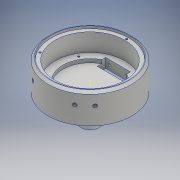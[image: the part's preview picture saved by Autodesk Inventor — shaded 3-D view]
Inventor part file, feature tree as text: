
AUTODESK INVENTOR PART (.ipt)
format: ipt  version: 2017 (Build 210142000, 142)  size: 281,088 bytes
history: native  units: mm
features: sketch x14, thread x10, extrude x7, plane x7, hole x7, projected_geometry x2, chamfer x1
ambient origin geometry x8: Origin, YZ Plane, XZ Plane, XY Plane, X Axis, Y Axis, Z Axis, Center Point
bodies: Solid1 (feature_tree)
feature tree (48):
  extrude  "Extrusion1"  Depth=25.0mm TaperAngle=0.0deg
  extrude  "Extrusion2"  Depth=17.0mm TaperAngle=0.0deg
  extrude  "Extrusion4"  Depth=35.0mm
  plane  "Work Plane1"
  extrude  "Extrusion7"  Depth=2.0mm TaperAngle=0.0deg
  chamfer  "Chamfer1"  Distance=2.0mm Angle=45.0deg
  hole  "Hole3"  [1 undecoded]
  hole  "Hole4"  [1 undecoded]
  thread  "Thread1"  [1 undecoded]
  thread  "Thread2"  [1 undecoded]
  thread  "Thread3"  [1 undecoded]
  thread  "Thread4"  [1 undecoded]
  thread  "Thread5"  [1 undecoded]
  thread  "Thread6"  [1 undecoded]
  sketch  "Sketch12"  dims[d54=1.6mm d55=6.0mm d56=4.0mm d57=2.0mm d58=90.0deg d59=5.0mm d60=20.594885mm d61=61.315mm d62=30.0mm d64=360.0deg]
  plane  "Work Plane2"
  plane  "Work Plane3"
  plane  "Work Plane4"
  plane  "Work Plane5"
  hole  "Hole5"  [1 undecoded]
  hole  "Hole6"  [1 undecoded]
  hole  "Hole9"  [1 undecoded]
  hole  "Hole10"  [1 undecoded]
  thread  "Thread7"  [1 undecoded]
  thread  "Thread8"  [1 undecoded]
  extrude  "Extrusion8"  Depth=14.5mm
  thread  "Thread11"  [1 undecoded]
  thread  "Thread12"  [1 undecoded]
  plane  "Work Plane6"
  sketch  "Sketch21"  dims[d88=3.0mm d89=6.0mm d90=4.0mm d91=2.0mm d92=90.0deg d93=4.0mm d94=20.594885mm d95=14.5mm]
  sketch  "Sketch22"  dims[d96=3.0mm d97=6.0mm d98=4.0mm d99=2.0mm d100=90.0deg d101=4.0mm d102=20.594885mm d117=10.0mm d118=0.0mm d119=10.0mm d120=0.0mm d125=15.0mm]
  extrude  "Extrusion10"  Depth=10.0mm TaperAngle=0.0deg
  hole  "Hole12"  [1 undecoded]
  plane  "Work Plane7"
  extrude  "Extrusion11"  Depth=5.0mm
  sketch  "Sketch1"  dims[d0=70.0mm d1=25.0mm d2=0.0mm]
  sketch  "Sketch2"  dims[d3=47.0mm d8=17.0mm d9=0.0mm]
  sketch  "Sketch8"  dims[d13=3.0mm d14=0.0mm d32=35.0mm]
  sketch  "Sketch10"  dims[d36=65.0mm d37=2.0mm d38=0.0mm d46=2.0mm d47=2.0mm d48=45.0deg]
  projected_geometry  "Projected Loop4"
  sketch  "Sketch11"  dims[d49=51.762mm d50=30.0mm d52=360.0deg]
  sketch  "Sketch13"  dims[d66=1.6mm d67=6.0mm d68=4.0mm d69=2.0mm d70=90.0deg d71=5.0mm d72=20.594885mm d73=10.0mm d74=0.0mm d75=10.0mm d76=0.0mm d77=10.0mm d78=0.0mm d79=10.0mm d80=0.0mm d81=10.0mm d82=0.0mm]
  sketch  "Sketch14"  dims[d83=10.0mm d84=0.0mm d85=6.981317mm]
  sketch  "Sketch17"  dims[d86=60.0deg d87=14.5mm]
  sketch  "Sketch23"  dims[d126=22.2mm d127=0.0mm d128=14.5mm d129=14.5mm]
  sketch  "Sketch24"  dims[d130=3.0mm d131=6.0mm d132=4.0mm d133=2.0mm d134=90.0deg d135=4.0mm d136=20.594885mm]
  sketch  "Sketch25"  dims[d137=3.0mm d138=6.0mm d139=4.0mm d140=2.0mm d141=90.0deg d142=4.0mm d143=20.594885mm d144=10.0mm d145=0.0mm d146=10.0mm d147=0.0mm d148=45.762433mm d164=35.0mm d173=58.5mm d175=47.2mm d176=21.0mm d177=7.0mm d178=10.0mm d179=0.0mm d180=15.0mm d181=2.1mm d182=2.1mm d183=4.1mm d184=4.1mm d185=7.5mm d186=7.5mm d187=2.1mm d188=6.0mm d189=4.0mm d190=2.0mm d191=90.0deg d192=8.0mm d193=20.594885mm d194=35.0mm d195=5.0mm d196=2.0mm d197=0.0mm d172=1.0mm]
  projected_geometry  "Projected Loop6"
note: 17 required parameter values undecoded (feature->parameter linkage not recoverable at this tier; creation-order binding heuristic only, values carry confidence <= 0.55)
